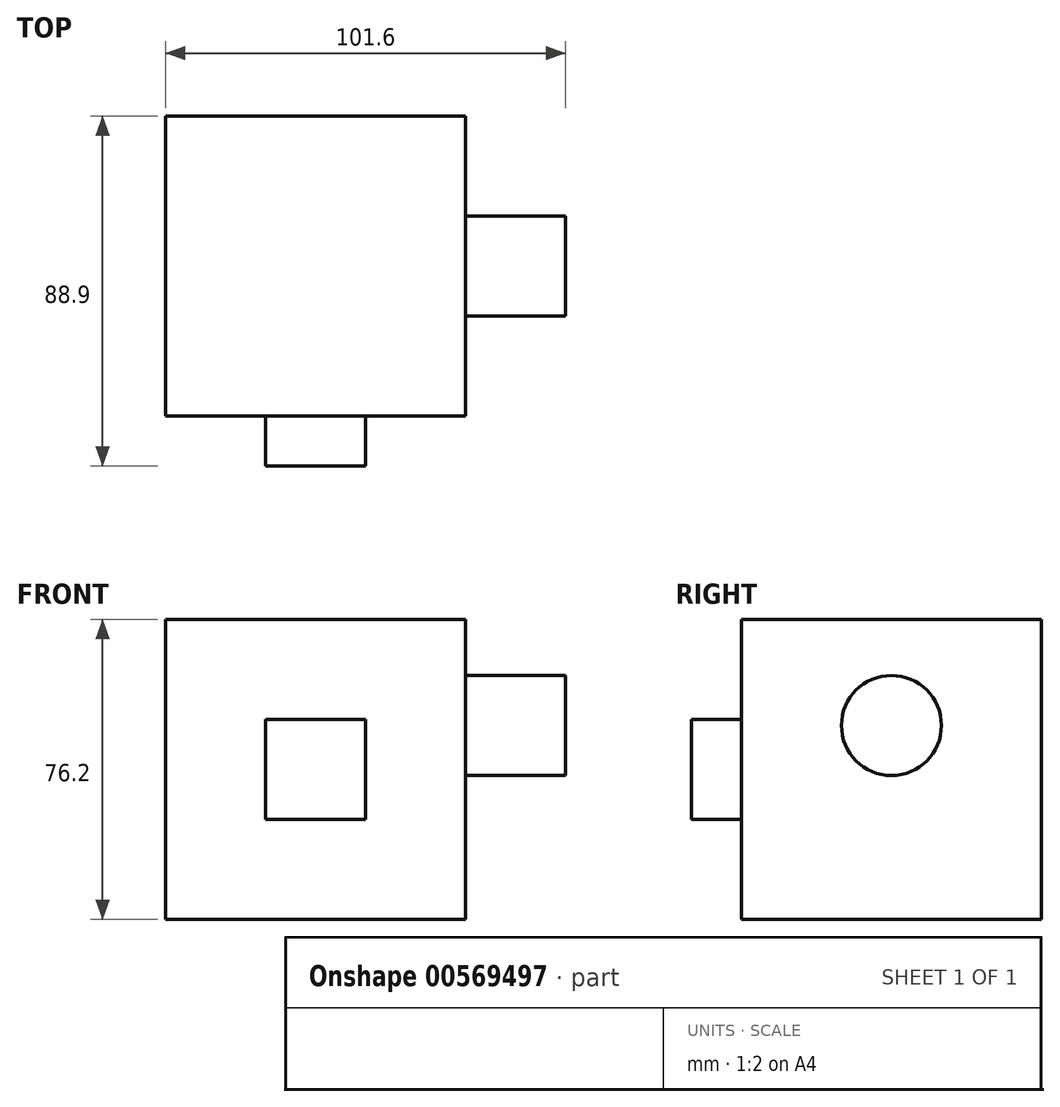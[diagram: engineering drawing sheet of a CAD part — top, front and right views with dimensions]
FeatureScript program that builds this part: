
annotation { "Feature Type Name" : "Feature", "Feature Type Description" : "" }
export const myFeature = defineFeature(function(context is Context, id is Id, definition is map)
    precondition{}
    {
        {
            var Q0;
            Q0=qCreatedBy(makeId("Front.planeOp"),FACE);
            var sketch = newSketch(context, id + "F0", { "sketchPlane" : qUnion([Q0])});
            skLineSegment(sketch, "E0.bottom", {"start": v(-63.28, 64.72) * mm, "end": v(12.92, 64.72) * mm});
            skLineSegment(sketch, "E0.top", {"start": v(-63.28, -11.48) * mm, "end": v(12.92, -11.48) * mm});
            skLineSegment(sketch, "E0.left", {"start": v(-63.28, 64.72) * mm, "end": v(-63.28, -11.48) * mm});
            skLineSegment(sketch, "E0.right", {"start": v(12.92, 64.72) * mm, "end": v(12.92, -11.48) * mm});
            skSolve(sketch);
        }
        {
            var Q0;
            Q0 = qSketchRegion(id + "F0", true);
            extrude(context, id + "F1", {"entities" : qUnion([Q0]), "depth" : 76.2 * mm, "offsetDistance" : 25.4 * mm});
        }
        {
            var Q0;
            Q0=makeQuery(id+"F1.opExtrude","CAP_FACE",FACE,{"disambiguationData":[OSD([sQuery(id+"F0.wireOp",EDGE,"E0.bottom"),sQuery(id+"F0.wireOp",EDGE,"E0.top"),sQuery(id+"F0.wireOp",EDGE,"E0.left"),sQuery(id+"F0.wireOp",EDGE,"E0.right")])],"isStart":false});
            var sketch = newSketch(context, id + "F2", { "sketchPlane" : qUnion([Q0])});
            skLineSegment(sketch, "E1.bottom", {"start": v(-37.88, 39.32) * mm, "end": v(-12.48, 39.32) * mm});
            skLineSegment(sketch, "E1.top", {"start": v(-37.88, 13.92) * mm, "end": v(-12.48, 13.92) * mm});
            skLineSegment(sketch, "E1.left", {"start": v(-37.88, 39.32) * mm, "end": v(-37.88, 13.92) * mm});
            skLineSegment(sketch, "E1.right", {"start": v(-12.48, 39.32) * mm, "end": v(-12.48, 13.92) * mm});
            skSolve(sketch);
        }
        {
            var Q0;
            Q0 = qSketchRegion(id + "F2", true);
            extrude(context, id + "F3", {"entities" : qUnion([Q0]), "operationType" : NewBodyOperationType.ADD, "depth" : 12.7 * mm, "offsetDistance" : 25.4 * mm});
        }
        {
            var Q0;
            Q0=makeQuery(id+"F1.opExtrude","SWEPT_FACE",FACE,{"disambiguationData":[OSD([sQuery(id+"F0.wireOp",EDGE,"E0.right")])]});
            var sketch = newSketch(context, id + "F4", { "sketchPlane" : qUnion([Q0])});
            skCircle(sketch, "E2", {"center": v(-38.1, 37.8) * mm, "radius": 12.7 * mm});
            skSolve(sketch);
        }
        {
            var Q0;
            Q0 = qSketchRegion(id + "F4", true);
            extrude(context, id + "F5", {"entities" : qUnion([Q0]), "operationType" : NewBodyOperationType.ADD, "depth" : 25.4 * mm, "offsetDistance" : 25.4 * mm});
        }
        {
            var Q0;
            Q0 = qSketchRegion(id + "F4", true);
            extrude(context, id + "F6", {"entities" : qUnion([Q0]), "operationType" : NewBodyOperationType.ADD, "depth" : 25.4 * mm, "offsetDistance" : 25.4 * mm});
        }
    });
